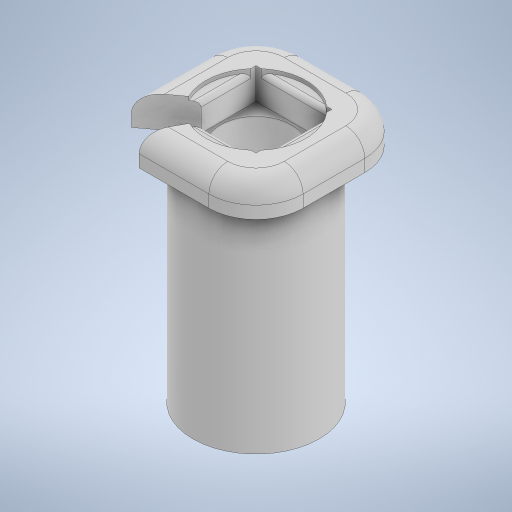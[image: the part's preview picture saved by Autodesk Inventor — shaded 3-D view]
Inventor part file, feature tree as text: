
AUTODESK INVENTOR PART (.ipt)
format: ipt  version: 2024.2 (Build 282272000, 272)  size: 356,352 bytes
history: native  units: in
note: dims shown in document units (in); Inventor stores cm internally (conversion verified against a paired STEP export)
features: extrude x6, sketch x6, fillet x3
ambient origin geometry x8: Origin, YZ Plane, XZ Plane, XY Plane, X Axis, Y Axis, Z Axis, Center Point
bodies: Solid1 (feature_tree)
feature tree (15):
  extrude  "Extrusion1"  Depth=1.6535in
  extrude  "Extrusion2"  Depth=0.8031in
  extrude  "Extrusion3"  Depth=0.2913in TaperAngle=0.0deg
  fillet  "Fillet4"  Radius=0.22in
  fillet  "Fillet5"  Radius=1.063in
  fillet  "Fillet6"  Radius=0.0394in
  extrude  "Extrusion4"  Depth=0.2in
  extrude  "Extrusion5"  Depth=0.05in
  extrude  "Extrusion7"  Depth=0.5118in TaperAngle=0.0deg
  sketch  "Sketch2"  dims[d1=1.6535in d2=1.6535in]
  sketch  "Sketch3"  dims[d3=0.2913in d4=0.0in d5=0.8031in]
  sketch  "Sketch4"  dims[d6=0.8031in d7=0.2913in d8=0.0in d9=0.22in d10=1.063in d11=0.0394in d12=0.0in]
  sketch  "Sketch5"  dims[d16=0.5in d17=0.2in]
  sketch  "Sketch6"  dims[d18=0.05in d19=1.3386in]
  sketch  "Sketch8"  dims[d20=0.7559in d21=0.5118in d22=0.0in d23=0.5118in d24=0.5906in d25=0.0in d29=0.2362in d30=1.2598in d31=0.0in d32=1.3386in]
